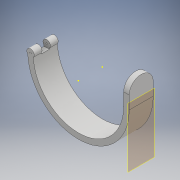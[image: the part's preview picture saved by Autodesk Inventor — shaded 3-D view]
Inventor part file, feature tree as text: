
AUTODESK INVENTOR PART (.ipt)
format: ipt  version: 2018.1 (Build 221171000, 171)  size: 179,712 bytes
history: native  units: mm
features: sketch x13, extrude x8, other x5, split x1, plane x1
ambient origin geometry x8: Origin, YZ Plane, XZ Plane, XY Plane, X Axis, Y Axis, Z Axis, Center Point
bodies: Body1 (feature_tree)
feature tree (28):
  other  "Sólido1"
  extrude  "Extrusión1"  Depth=24.5mm
  extrude  "Extrusión2"  Depth=13.0mm
  sketch  "Boceto3"  dims[d5=4.35mm d6=0.0mm d7=0.1mm]
  other  "Engrosado1"
  extrude  "Extrusión3"  Depth=0.1mm
  sketch  "Boceto4"  dims[d8=0.1mm d9=4.25mm d10=0.0mm]
  split  "Dividir1"
  other  "Engrosado2"
  extrude  "Extrusión4"  Depth=4.25mm TaperAngle=0.0deg
  sketch  "Boceto6"  dims[d13=3.0mm d14=12.0mm d15=0.0mm]
  extrude  "Extrusión5"  Depth=3.0mm
  sketch  "Boceto8"  dims[d19=3.0mm d20=0.0mm d21=3.0mm d22=0.0mm]
  sketch  "Boceto9"  dims[d23=5.0mm]
  sketch  "Boceto10"  dims[d24=1.6mm d25=0.0mm]
  plane  "Plano de trabajo1"
  extrude  "Extrusión6"  Depth=3.0mm TaperAngle=0.0deg
  extrude  "Extrusión7"  Depth=4.25mm
  extrude  "Extrusión8"  Depth=3.0mm TaperAngle=0.0deg
  other  "Engrosado3"
  other  "Engrosado4"
  sketch  "Boceto1"  dims[d0=27.5mm d1=24.5mm]
  sketch  "Boceto2"  dims[d2=13.0mm d3=0.0mm d4=4.0mm]
  sketch  "Boceto5"  dims[d11=0.8mm d12=3.0mm]
  sketch  "Boceto7"  dims[d16=4.25mm d17=0.0mm d18=7.0mm]
  sketch  "Boceto11"  dims[d26=0.5mm]
  sketch  "Boceto12"  dims[d27=0.5mm]
  sketch  "Boceto13"  dims[d28=0.5mm d29=0.5mm]
